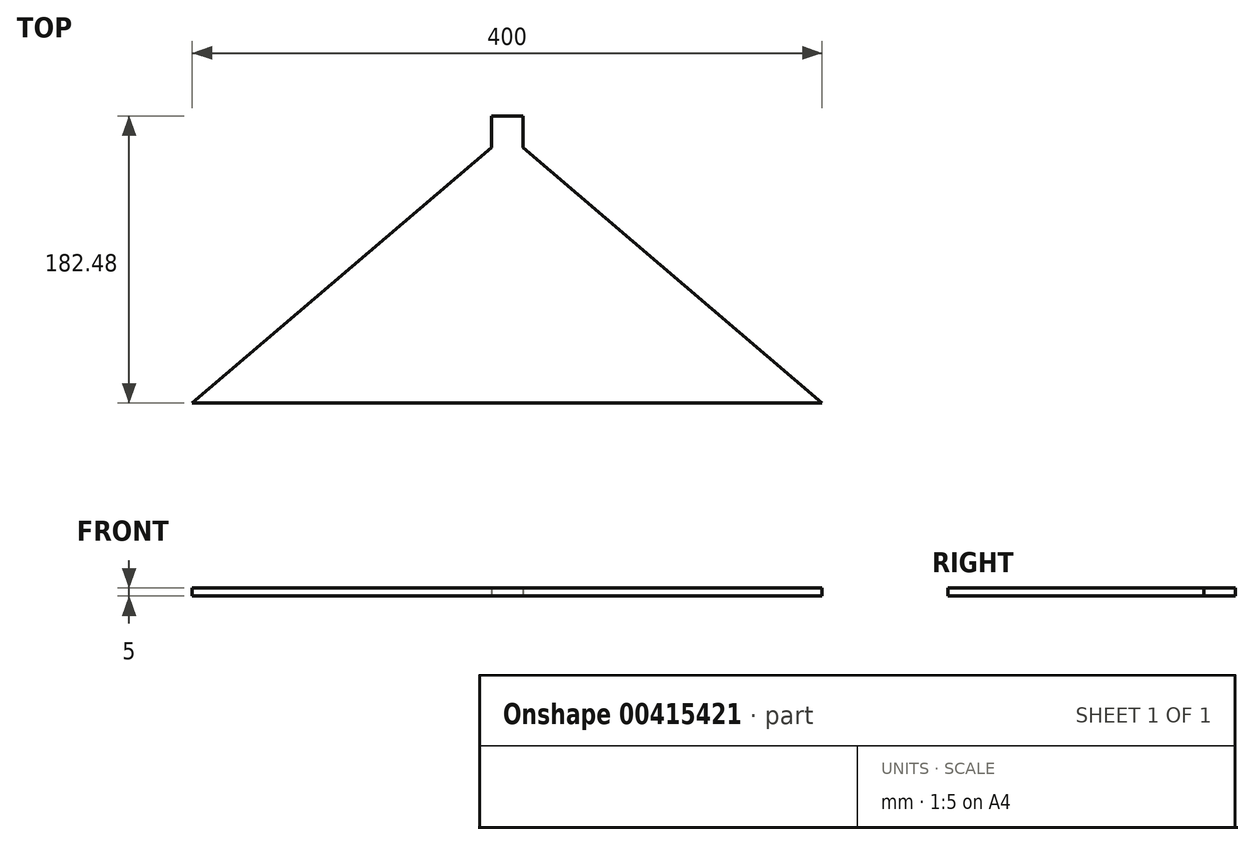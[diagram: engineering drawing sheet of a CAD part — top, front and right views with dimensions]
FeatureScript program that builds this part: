
annotation { "Feature Type Name" : "Feature", "Feature Type Description" : "" }
export const myFeature = defineFeature(function(context is Context, id is Id, definition is map)
    precondition{}
    {
        {
            var Q0;
            Q0=qCreatedBy(makeId("Top.planeOp"),FACE);
            var sketch = newSketch(context, id + "F0", { "sketchPlane" : qUnion([Q0])});
            skLineSegment(sketch, "E0", {"start": v(-200, -51.25) * mm, "end": v(200, -51.25) * mm});
            skLineSegment(sketch, "E1", {"start": v(10, 111.23) * mm, "end": v(200, -51.25) * mm});
            skLineSegment(sketch, "E2.MirrorCS", {"start": v(-10, 111.23) * mm, "end": v(-200, -51.25) * mm});
            skLineSegment(sketch, "E3", {"start": v(-10, 111.23) * mm, "end": v(-10, 131.23) * mm});
            skLineSegment(sketch, "E4", {"start": v(-10, 131.23) * mm, "end": v(10, 131.23) * mm});
            skLineSegment(sketch, "E5", {"start": v(10, 111.23) * mm, "end": v(10, 131.23) * mm});
            skPoint(sketch, "E6.MirrorCS.start.orphan", {"position": v(0, 111.23) * mm});
            skPoint(sketch, "E7.start.orphan", {"position": v(0, -51.25) * mm});
            skSolve(sketch);
        }
        {
            var Q0;
            Q0=makeQuery(id+"F0.imprint","IMPRINT",FACE,{"disambiguationData":[TD([[makeQuery(id+"F0.imprint","IMPRINT",EDGE,{"derivedFrom":sQuery(id+"F0.wireOp",EDGE,"E0")}),1.0]])]});
            extrude(context, id + "F1", {"entities" : qUnion([Q0]), "depth" : 5 * mm});
        }
    });
